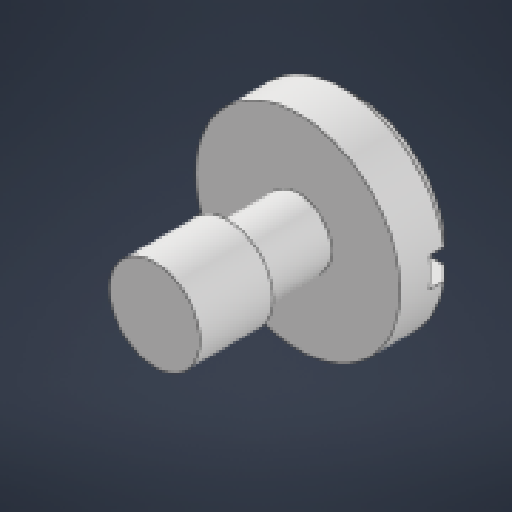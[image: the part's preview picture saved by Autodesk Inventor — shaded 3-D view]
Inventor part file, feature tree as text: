
AUTODESK INVENTOR PART (.ipt)
format: ipt  version: 2023 (Build 270158000, 158)  size: 149,504 bytes
history: native  units: in
note: dims shown in document units (in); Inventor stores cm internally (conversion verified against a paired STEP export)
features: extrude x4, sketch x2, chamfer x1
ambient origin geometry x8: Origin, YZ Plane, XZ Plane, XY Plane, X Axis, Y Axis, Z Axis, Center Point
bodies: Solid1 (feature_tree)
feature tree (7):
  sketch  "Sketch1"  dims[d0=0.5512in d1=0.1811in]
  extrude  "Extrusion1"  Depth=0.1811in
  extrude  "Extrusion2"  Depth=0.1598in TaperAngle=0.0deg
  extrude  "Extrusion3"  Depth=0.1598in TaperAngle=0.0deg
  extrude  "Extrusion4"  Depth=0.1598in TaperAngle=0.0deg
  chamfer  "Chamfer1"  Distance=0.0787in
  sketch  "Sketch2"  dims[d2=0.2449in d3=0.1598in d4=0.0in d5=0.3866in d6=0.0in d7=0.1898in d8=0.0in d9=0.0787in d10=0.0787in d11=0.0in d12=0.0394in d13=0.0787in d14=45.0deg]
